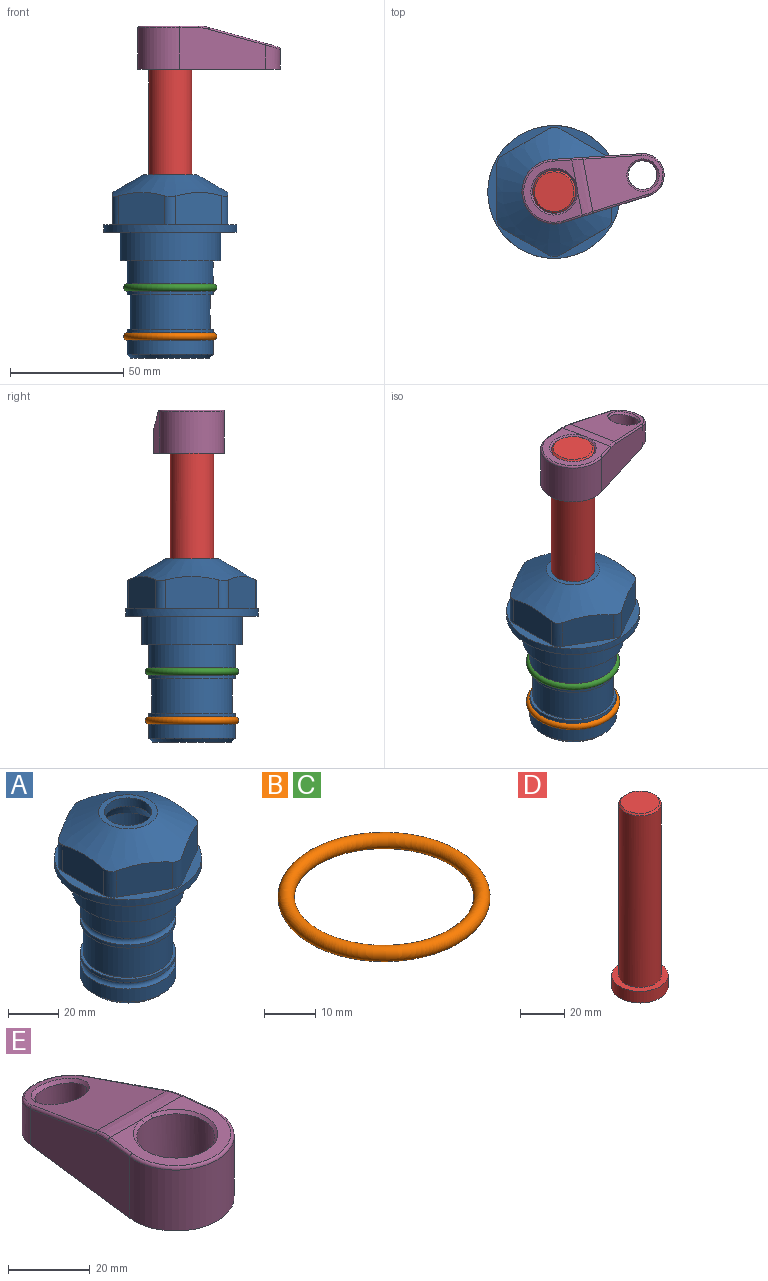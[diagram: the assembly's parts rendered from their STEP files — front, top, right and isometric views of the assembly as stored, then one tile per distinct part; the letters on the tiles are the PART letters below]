
ASSEMBLY  parts=5 mates=4
PART A: 36 faces, bbox 58.7x58.7x81 mm
  f0: cylinder r=17.78mm len=35.56mm, axis (0,0,1), area 1670.8mm2, adj f23,f24,f31
  f1: cylinder r=19.05mm len=38.1mm, axis (0,0,1), area 1191.9mm2, adj f26,f27,f30
  f2: plane 58.66x58.66mm, normal (0,0,-1), area 1150.6mm2, adj f3,f28
  f3: cylinder r=29.33mm len=58.66mm, axis (0,0,-1), area 585.1mm2, adj f2,f4
  f4: plane 58.66x58.66mm, normal (0,0,1), area 475.9mm2, adj f3,f5,f6,f7,f8,f9,f10,f11
  f5: plane 20.32x14.34mm, normal (-0.5,0.87,0), area 324.4mm2, adj f4,f15,f16,f17
  f6: plane 20.32x14.34mm, normal (0.5,0.87,0), area 324.4mm2, adj f4,f14,f15,f17
  f7: plane 23.48x14.34mm, normal (1,0,0), area 324.4mm2, adj f4,f13,f14,f17
  f8: plane 20.32x14.34mm, normal (0.5,-0.87,0), area 324.4mm2, adj f4,f12,f13,f17
  f9: plane 20.32x14.34mm, normal (-0.5,-0.87,0), area 324.4mm2, adj f4,f11,f12,f17
  f10: plane 23.48x14.34mm, normal (-1,0,0), area 324.4mm2, adj f4,f11,f16,f17
  f11: cylinder r=5.08mm len=12.85mm, axis (0,0,-1), area 67.2mm2, adj f4,f9,f10,f17
  f12: cylinder r=5.08mm len=12.85mm, axis (0,0,-1), area 67.2mm2, adj f4,f8,f9,f17
  f13: cylinder r=5.08mm len=12.85mm, axis (0,0,-1), area 67.2mm2, adj f4,f7,f8,f17
  f14: cylinder r=5.08mm len=12.85mm, axis (0,0,-1), area 67.2mm2, adj f4,f6,f7,f17
  f15: cylinder r=5.08mm len=12.85mm, axis (0,0,-1), area 67.2mm2, adj f4,f5,f6,f17
  f16: cylinder r=5.08mm len=12.85mm, axis (0,0,-1), area 67.2mm2, adj f4,f5,f10,f17
  f17: cone r=11.73mm half-angle=60deg, axis (0,0,-1), area 2071.8mm2, adj f5,f6,f7,f8,f9,f10,f11,f12
  f18: plane 23.46x23.46mm, normal (0,0,1), area 147.4mm2, adj f17,f35
  f19: plane 34.93x34.93mm, normal (0,0,-1), area 958mm2, adj f29
  f20: cylinder r=19.05mm len=38.1mm, axis (0,0,1), area 760.1mm2, adj f21,f29
  f21: torus R=19.05mm, axis (0,0,1), area 565.3mm2, adj f20,f22
  f22: cylinder r=19.05mm len=38.1mm, axis (0,0,1), area 190mm2, adj f21,f23
  f23: plane 38.1x38.1mm, normal (0,0,1), area 146.9mm2, adj f0,f22
  f24: plane 38.1x38.1mm, normal (0,0,-1), area 146.9mm2, adj f0,f25
  f25: cylinder r=19.05mm len=38.1mm, axis (0,0,1), area 190mm2, adj f24,f26
  f26: torus R=19.05mm, axis (0,0,1), area 565.3mm2, adj f1,f25
  f27: plane 44.45x44.45mm, normal (0,0,-1), area 411.7mm2, adj f1,f28
  f28: cylinder r=22.23mm len=44.45mm, axis (0,0,1), area 1773.5mm2, adj f2,f27
  f29: cone r=19.05mm half-angle=45deg, axis (0,0,1), area 257.5mm2, adj f19,f20
  f30: cylinder r=3.17mm len=6.75mm, axis (-1,0,0), area 128mm2, adj f1,f33
  f31: cylinder r=3.17mm len=6.35mm, axis (-1,0,0), area 102.5mm2, adj f0,f33
  f32: plane 25.4x25.4mm, normal (0,0,1), area 506.7mm2, adj f33
  f33: cylinder r=12.7mm len=66.42mm, axis (0,0,-1), area 5236.2mm2, adj f30,f31,f32,f34
  f34: cone r=9.53mm half-angle=30deg, axis (0,0,-1), area 443.4mm2, adj f33,f35
  f35: cylinder r=9.53mm len=19.05mm, axis (0,0,-1), area 240.9mm2, adj f18,f34
PART B: 1 faces, bbox 44.7x44.7x3.2 mm
  f0: torus R=19.05mm, axis (0,0,1), area 1193.9mm2
PART C: same geometry as B
PART D: 6 faces, bbox 25.4x25.4x101.6 mm
  f0: plane 17.46x17.46mm, normal (0,0,1), area 239.5mm2, adj f5
  f1: plane 25.4x25.4mm, normal (0,0,-1), area 506.7mm2, adj f2
  f2: cylinder r=12.7mm len=25.4mm, axis (0,0,1), area 506.7mm2, adj f1,f3
  f3: plane 25.4x25.4mm, normal (0,0,1), area 221.7mm2, adj f2,f4
  f4: cylinder r=9.53mm len=94.46mm, axis (0,0,1), area 5653mm2, adj f3,f5
  f5: cone r=8.73mm half-angle=45deg, axis (0,0,-1), area 64.4mm2, adj f0,f4
PART E: 31 faces, bbox 31.7x65.5x19.8 mm
  f0: plane 39.12x18.26mm, normal (0.99,0.12,0), area 612.2mm2, adj f1,f4,f7,f11,f13,f15
  f1: cylinder r=9.53mm len=18.91mm, axis (0,0,-1), area 296.1mm2, adj f0,f2,f7,f17
  f2: plane 39.12x18.26mm, normal (-0.99,0.12,0), area 612.2mm2, adj f1,f4,f7,f12,f14,f16
  f3: cylinder r=6.35mm len=12.7mm, axis (0,0,-1), area 362.4mm2, adj f7,f18
  f4: cylinder r=14.29mm len=28.58mm, axis (0,0,-1), area 882.2mm2, adj f0,f2,f7,f10
  f5: cylinder r=9.53mm len=19.05mm, axis (0,0,-1), area 1092.6mm2, adj f7,f19,f20
  f6: plane 26.99x23.69mm, normal (0,0,1), area 216.2mm2, adj f9,f10,f11,f12,f19
  f7: plane 63.5x28.58mm, normal (0,0,-1), area 661.8mm2, adj f0,f1,f2,f3,f4,f5,f22,f23
  f8: plane 33.52x23.6mm, normal (0,0.26,0.97), area 486mm2, adj f9,f15,f16,f17,f18
  f9: cylinder r=19.05mm len=24.72mm, axis (1,0,0), area 120.4mm2, adj f6,f8,f13,f14,f20
  f10: torus R=13.49mm, axis (0,0,1), area 59mm2, adj f4,f6,f11,f12
  f11: cylinder r=0.79mm len=8.67mm, axis (0.12,-0.99,0), area 10.8mm2, adj f0,f6,f10,f13
  f12: cylinder r=0.79mm len=8.67mm, axis (0.12,0.99,0), area 10.8mm2, adj f2,f6,f10,f14
  f13: bspline ~4.95x1.42mm, area 6.1mm2, adj f0,f9,f11,f15
  f14: bspline ~4.95x1.42mm, area 6.1mm2, adj f2,f9,f12,f16
  f15: cylinder r=0.79mm len=25.95mm, axis (0.12,-0.96,0.26), area 32.9mm2, adj f0,f8,f13,f17
  f16: cylinder r=0.79mm len=25.95mm, axis (0.12,0.96,-0.26), area 32.9mm2, adj f2,f8,f14,f17
  f17: bspline ~18.91x8.38mm, area 30mm2, adj f1,f8,f15,f16
  f18: bspline ~14.29x14.29mm, area 48.3mm2, adj f3,f8
  f19: cone r=9.53mm half-angle=45deg, axis (0,0,1), area 66.5mm2, adj f5,f6,f20
  f20: bspline ~3.22x0.96mm, area 3.5mm2, adj f5,f9,f19
  f21: plane 2.75x2.72mm, normal (0,0,-1), area 2.9mm2, adj f23,f25,f28
  f22: plane 23.05x15.88mm, normal (-0.99,-0.12,0), area 323.6mm2, adj f7,f25,f26,f27,f28,f29
  f23: plane 23.05x15.88mm, normal (0.99,-0.12,0), area 323.6mm2, adj f7,f21,f25,f27,f28,f30
  f24: cylinder r=9.53mm len=10.69mm, axis (0,0,-1), area 114.7mm2, adj f7,f27,f29,f30
  f25: cylinder r=12.7mm len=20.59mm, axis (0,0,-1), area 381.1mm2, adj f7,f21,f22,f23,f26,f28
  f26: plane 2.75x2.72mm, normal (0,0,-1), area 2.9mm2, adj f22,f25,f28
  f27: plane 19.72x18.37mm, normal (0,-0.26,-0.97), area 291.8mm2, adj f22,f23,f24,f28,f29,f30
  f28: cylinder r=15.88mm len=19.92mm, axis (1,0,0), area 54.8mm2, adj f21,f22,f23,f25,f26,f27
  f29: cylinder r=1.59mm len=11mm, axis (0,0,-1), area 34.7mm2, adj f7,f22,f24,f27
  f30: cylinder r=1.59mm len=11mm, axis (0,0,-1), area 34.7mm2, adj f7,f23,f24,f27
PLACE A at identity fixed
PLACE B t=(0,0,-21.59)mm
PLACE C at identity
PLACE D rot(axis=(0,0,-1),79.4deg) t=(0,0,27.55)mm
PLACE E rot(axis=(0,0,-1),79.4deg) t=(0,0,27.55)mm
MATE fastened A.f0 <-> C.f0  axis (0,0,1) through (0,0,-24.51)mm
MATE cylindrical D.f2 <-> A.f0  axis (0,0,-1) through (0,0,-10.55)mm
MATE fastened A.f0 <-> B.f0  axis (0,0,1) through (0,0,-46.1)mm
MATE fastened D.f2 <-> E.f4  axis (0,0,1) through (0,0,91.05)mm
